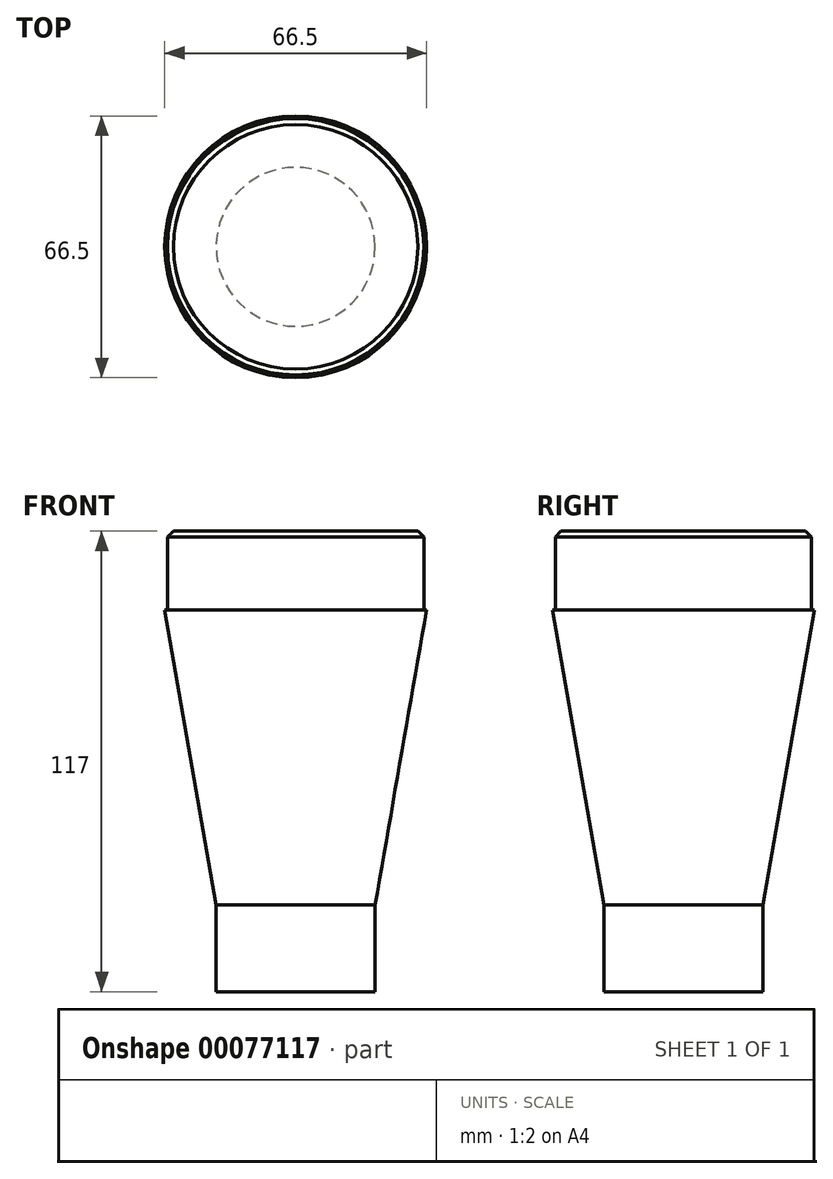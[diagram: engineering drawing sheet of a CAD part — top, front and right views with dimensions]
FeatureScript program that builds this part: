
annotation { "Feature Type Name" : "Feature", "Feature Type Description" : "" }
export const myFeature = defineFeature(function(context is Context, id is Id, definition is map)
    precondition{}
    {
        {
            var Q0;
            Q0=qCreatedBy(makeId("Front.planeOp"),FACE);
            var sketch = newSketch(context, id + "F0", { "sketchPlane" : qUnion([Q0])});
            skLineSegment(sketch, "E0", {"start": v(-32.55, 63.27) * mm, "end": v(-32.55, 43.27) * mm});
            skLineSegment(sketch, "E1", {"start": v(-32.55, 43.27) * mm, "end": v(-33.25, 43.27) * mm});
            skLineSegment(sketch, "E2", {"start": v(-33.25, 43.27) * mm, "end": v(-20.2, -31.73) * mm});
            skLineSegment(sketch, "E3", {"start": v(-20.2, -31.73) * mm, "end": v(-20.2, -53.73) * mm});
            skLineSegment(sketch, "E4", {"start": v(-20.2, -53.73) * mm, "end": v(0, -53.73) * mm});
            skLineSegment(sketch, "E5", {"start": v(-32.55, 63.27) * mm, "end": v(0, 63.27) * mm});
            skLineSegment(sketch, "E6", {"start": v(0, 94.78) * mm, "end": v(0, -99.97) * mm, "construction": true});
            skLineSegment(sketch, "E7", {"start": v(0, 63.27) * mm, "end": v(0, -53.73) * mm});
            skSolve(sketch);
        }
        {
            var Q0;
            Q0=makeQuery(id+"F0.imprint","IMPRINT",FACE,{"disambiguationData":[TD([[makeQuery(id+"F0.imprint","IMPRINT",EDGE,{"derivedFrom":sQuery(id+"F0.wireOp",EDGE,"E0")}),1.0]])]});
            var Q1;
            Q1=sQuery(id+"F0.wireOp",EDGE,"E6");
            revolve(context, id + "F1", {"entities" : qUnion([Q0]), "axis" : qUnion([Q1]), "revolveType" : RevolveType.FULL});
        }
        {
            var Q0;
            Q0=makeQuery(id+"F1.opRevolve","SWEPT_EDGE",EDGE,{"disambiguationData":[OSD([sQuery(id+"F0.wireOp",EDGE,"E0"),sQuery(id+"F0.wireOp",EDGE,"E5")])]});
            chamfer(context, id + "F2", {"entities" : qUnion([Q0]), "width" : 1.5 * mm, "tangentPropagation" : true});
        }
    });
